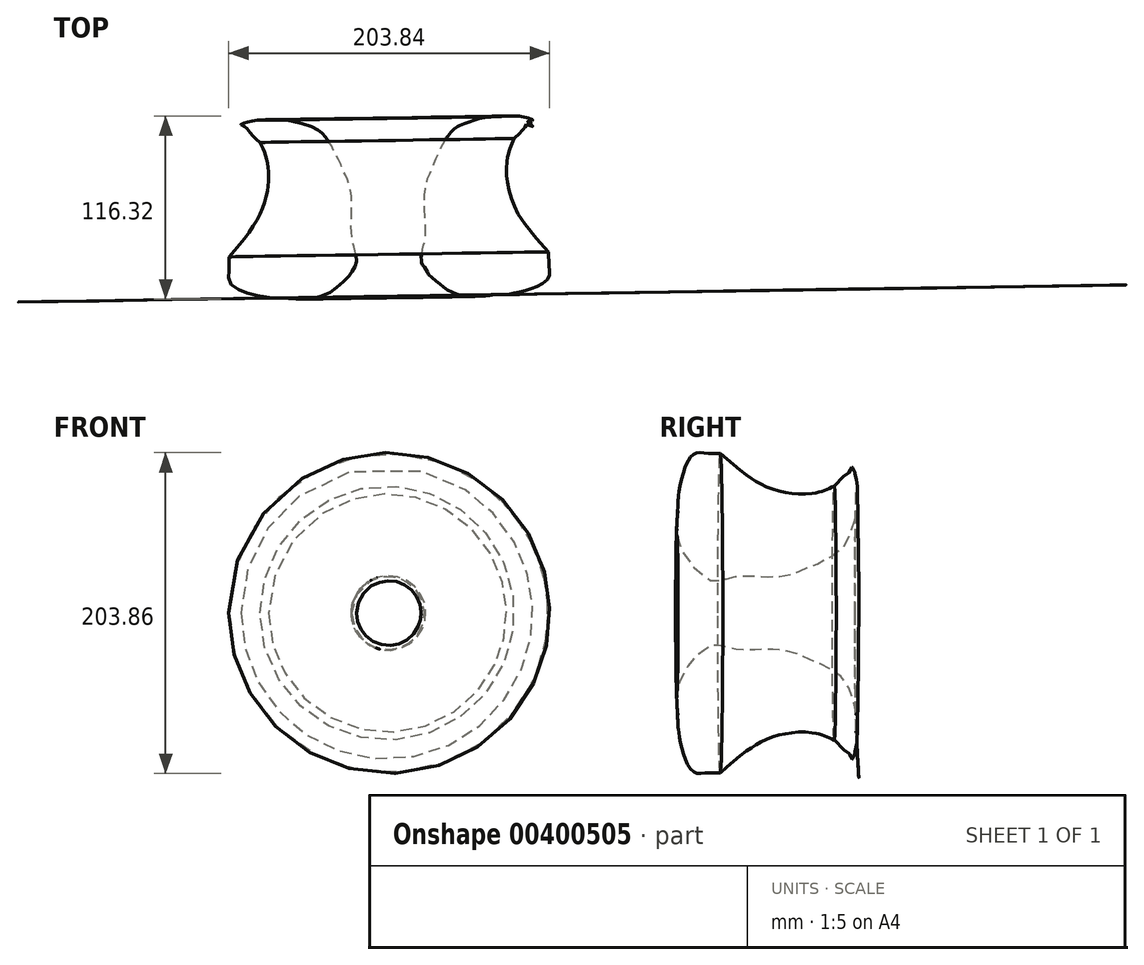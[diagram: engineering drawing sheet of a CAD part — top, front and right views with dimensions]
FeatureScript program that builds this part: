
annotation { "Feature Type Name" : "Feature", "Feature Type Description" : "" }
export const myFeature = defineFeature(function(context is Context, id is Id, definition is map)
    precondition{}
    {
        {
            var Q0;
            Q0=qCreatedBy(makeId("Top.planeOp"),FACE);
            var sketch = newSketch(context, id + "F0", { "sketchPlane" : qUnion([Q0])});
            skFitSpline(sketch, "E0", {"points": [v(-26.91, 40.37) * mm, v(-23.98, 34.01) * mm, v(-21.78, 25.2) * mm, v(-21.78, 13.21) * mm, v(-27.16, -5.87) * mm, v(-46.49, -32.3) * mm], "startDerivative": vector(22.56, -44.3) * mm, "endDerivative": vector(-76, -89.82) * mm});
            skFitSpline(sketch, "E1", {"points": [v(-46.49, -32.3) * mm, v(-46.49, -38.66) * mm, v(-46.49, -41.84) * mm, v(-46.49, -47.71) * mm, v(-41.6, -52.6) * mm, v(-32.3, -56.03) * mm, v(-22.51, -57.99) * mm, v(-17.62, -58.48) * mm, v(-11.26, -58.48) * mm, v(-5.14, -58.97) * mm, v(0, -58.97) * mm, v(5.87, -58.97) * mm, v(17.62, -54.8) * mm, v(23.24, -50.4) * mm, v(29.36, -45.02) * mm, v(31.07, -42.33) * mm, v(33.28, -38.66) * mm, v(34.26, -37.2) * mm, v(34.26, -32.3) * mm, v(33.52, -29.12) * mm, v(32.79, -25.7) * mm, v(32.05, -23.42) * mm, v(31.07, -16.88) * mm, v(31.07, -11.99) * mm, v(31.07, -10.28) * mm, v(31.32, -3.18) * mm, v(31.32, 3.91) * mm, v(31.07, 7.1) * mm, v(29.36, 14.68) * mm, v(28.14, 18.1) * mm, v(25.45, 23.49) * mm, v(23.24, 29.12) * mm, v(20.55, 34.01) * mm, v(18.35, 38.41) * mm, v(15.41, 42.82) * mm, v(12.23, 46.49) * mm, v(7.34, 49.67) * mm, v(-6.12, 53.83) * mm, v(-9.54, 54.32) * mm, v(-13.7, 54.56) * mm, v(-18.6, 54.56) * mm, v(-24.22, 54.56) * mm, v(-29.36, 54.56) * mm, v(-34.01, 53.58) * mm, v(-36.21, 53.1) * mm, v(-38.98, 51.87) * mm, v(-38.98, 51.63) * mm, v(-35.72, 49.67) * mm, v(-35.23, 48.94) * mm, v(-32.3, 45.51) * mm, v(-30.1, 43.06) * mm, v(-26.91, 40.37) * mm], "startDerivative": vector(-3.3, -316.17) * mm, "endDerivative": vector(191.61, -152.63) * mm});
            skLineSegment(sketch, "E2", {"start": v(53.58, 55.54) * mm, "end": v(55.3, -55.54) * mm});
            skSolve(sketch);
        }
        {
            var Q0;
            Q0=makeQuery(id+"F0.imprint","IMPRINT",FACE,{"disambiguationData":[TD([[makeQuery(id+"F0.imprint","IMPRINT",EDGE,{"derivedFrom":sQuery(id+"F0.wireOp",EDGE,"E0")}),1.0]])]});
            var Q1;
            Q1=sQuery(id+"F0.wireOp",EDGE,"E2");
            revolve(context, id + "F1", {"entities" : qUnion([Q0]), "axis" : qUnion([Q1]), "revolveType" : RevolveType.FULL});
        }
    });
